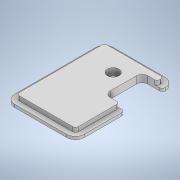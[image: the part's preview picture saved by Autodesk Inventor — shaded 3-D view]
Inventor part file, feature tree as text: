
AUTODESK INVENTOR PART (.ipt)
format: ipt  version: 2021 (Build 250183000, 183)  size: 160,768 bytes
history: native  units: mm
features: extrude x3, fillet x3, sketch x3
ambient origin geometry x8: Origin, YZ Plane, XZ Plane, XY Plane, X Axis, Y Axis, Z Axis, Center Point
bodies: Solid1 (feature_tree)
feature tree (9):
  extrude  "Extrusion1"  Depth=17.0mm
  extrude  "Extrusion2"  Depth=15.2mm
  fillet  "Fillet1"  Radius=10.2mm
  fillet  "Fillet2"  Radius=0.75mm
  extrude  "Extrusion3"  Depth=0.5mm
  fillet  "Fillet3"  Radius=6.5mm
  sketch  "Sketch1"  dims[d0=12.0mm d1=17.0mm]
  sketch  "Sketch2"  dims[d2=0.5mm d3=0.0mm d4=15.2mm d5=10.2mm d6=0.75mm d7=0.0mm]
  sketch  "Sketch3"  dims[d8=1.5mm d9=0.5mm d10=6.5mm d11=2.5mm d12=2.0mm d13=3.5mm d14=6.0mm d15=4.5mm d16=2.0mm d17=1.0mm d18=1.0mm d19=0.0mm d20=0.5mm]
